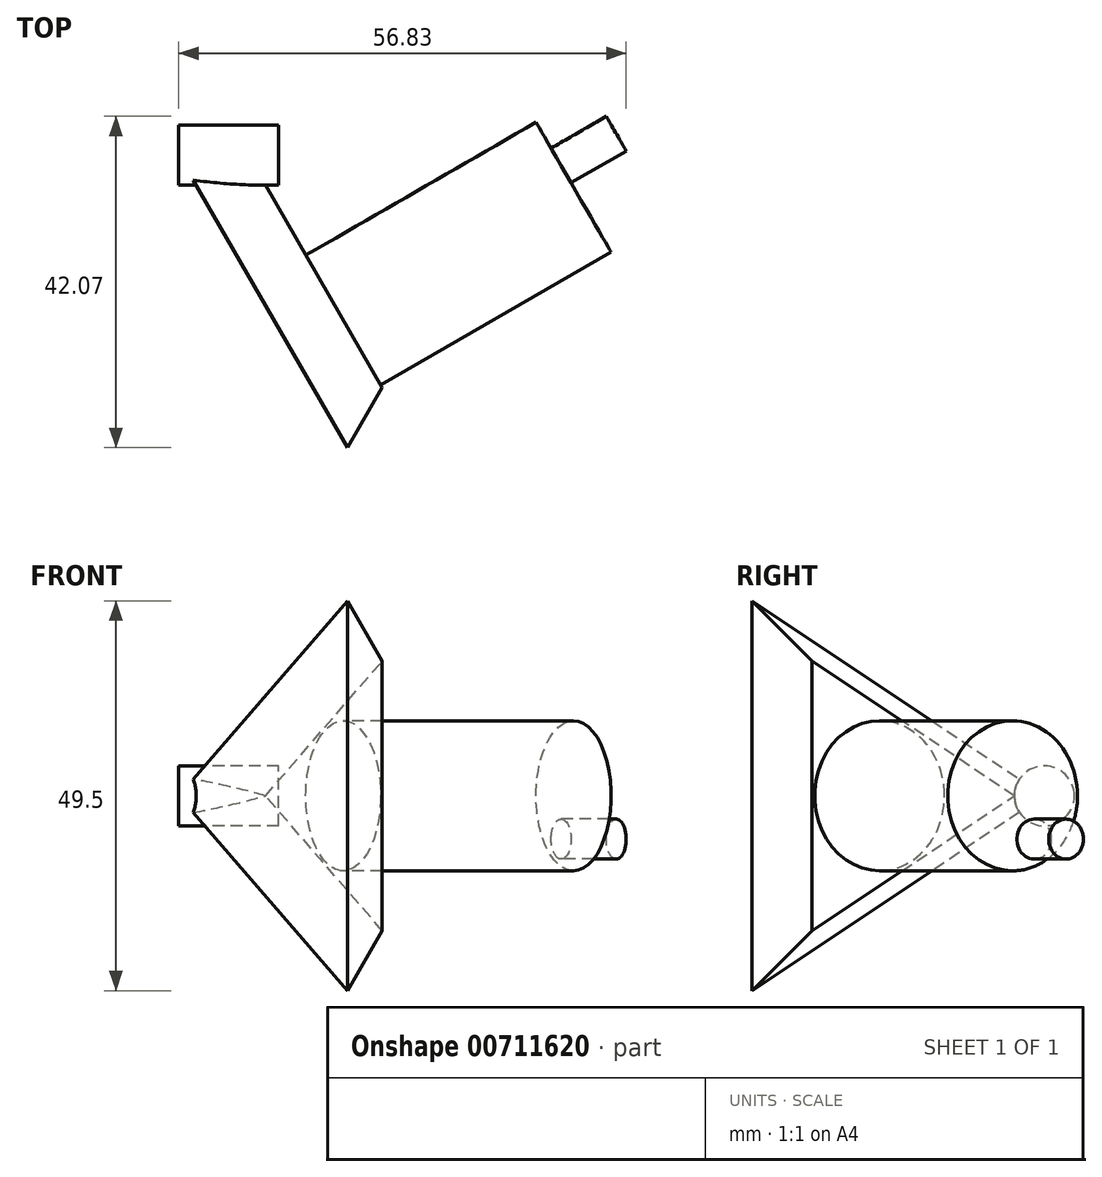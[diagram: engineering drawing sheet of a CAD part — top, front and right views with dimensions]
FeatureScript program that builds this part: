
annotation { "Feature Type Name" : "Feature", "Feature Type Description" : "" }
export const myFeature = defineFeature(function(context is Context, id is Id, definition is map)
    precondition{}
    {
        {
            var Q0;
            Q0=qCreatedBy(makeId("Top.planeOp"),FACE);
            var sketch = newSketch(context, id + "F0", { "sketchPlane" : qUnion([Q0])});
            skArc(sketch, "E0", {"start": v(0, 0) * mm, "mid": v(2.6, -19.72) * mm, "end": v(10.2, -38.1) * mm});
            skLineSegment(sketch, "E1", {"start": v(10.2, -38.1) * mm, "end": v(76.2, 0) * mm, "construction": true});
            skSolve(sketch);
        }
        {
            var Q0;
            Q0=qCreatedBy(makeId("Right.planeOp"),FACE);
            cPlane(context, id + "F1", {"entities" : qUnion([Q0]), "cplaneType" : CPlaneType.OFFSET, "offset" : 19.05 * mm, "width" : 152.4 * mm, "height" : 152.4 * mm});
        }
        {
            var Q0;
            Q0=qCreatedBy(id+"F1.planeOp",FACE);
            var sketch = newSketch(context, id + "F2", { "sketchPlane" : qUnion([Q0])});
            skCircle(sketch, "E2", {"center": v(0, 0) * mm, "radius": 3.81 * mm});
            skSolve(sketch);
        }
        {
            var Q0;
            Q0=qCreatedBy(makeId("Top.planeOp"),FACE);
            var sketch = newSketch(context, id + "F3", { "sketchPlane" : qUnion([Q0])});
            skLineSegment(sketch, "E3", {"start": v(19.05, 0) * mm, "end": v(33.34, -24.75) * mm});
            skLineSegment(sketch, "E4", {"start": v(33.34, -24.75) * mm, "end": v(76.2, 0) * mm, "construction": true});
            skLineSegment(sketch, "E5", {"start": v(76.2, 0) * mm, "end": v(19.05, 0) * mm, "construction": true});
            skSolve(sketch);
        }
        {
            var Q0;
            Q0=qCreatedBy(makeId("Top.planeOp"),FACE);
            var Q1;
            Q1=sQuery(id+"F3.wireOp",EDGE,"E3");
            cPlane(context, id + "F4", {"entities" : qUnion([Q0, Q1]), "cplaneType" : CPlaneType.LINE_ANGLE, "offset" : 25.4 * mm, "angle" : 90 * degree, "width" : 152.4 * mm, "height" : 152.4 * mm});
        }
        {
            var Q0;
            Q0=qCreatedBy(id+"F4.planeOp",FACE);
            var sketch = newSketch(context, id + "F5", { "sketchPlane" : qUnion([Q0])});
            skCircle(sketch, "E6.cCircle", {"center": v(-38.1, 0) * mm, "radius": 14.29 * mm, "construction": true});
            skLineSegment(sketch, "E6.0", {"start": v(-9.53, 0) * mm, "end": v(-52.39, -24.75) * mm});
            skLineSegment(sketch, "E6.1", {"start": v(-52.39, -24.75) * mm, "end": v(-52.39, 24.75) * mm});
            skLineSegment(sketch, "E6.2", {"start": v(-52.39, 24.75) * mm, "end": v(-9.53, 0) * mm});
            skPoint(sketch, "E6.0.midPoint", {"position": v(-30.96, -12.37) * mm});
            skSolve(sketch);
        }
        {
            var Q0;
            Q0=makeQuery(id+"F5.imprint","IMPRINT",FACE,{"disambiguationData":[TD([[makeQuery(id+"F5.imprint","IMPRINT",EDGE,{"derivedFrom":sQuery(id+"F5.wireOp",EDGE,"E6.0")}),-1.0]])]});
            extrude(context, id + "F6", {"entities" : qUnion([Q0]), "depth" : 7.62 * mm, "offsetDistance" : 25.4 * mm});
        }
        {
            var Q0;
            Q0=makeQuery(id+"F6.opExtrude","CAP_FACE",FACE,{"disambiguationData":[OSD([sQuery(id+"F5.wireOp",EDGE,"E6.0"),sQuery(id+"F5.wireOp",EDGE,"E6.1"),sQuery(id+"F5.wireOp",EDGE,"E6.2")])],"isStart":false});
            chamfer(context, id + "F7", {"entities" : qUnion([Q0]), "chamferType" : ChamferType.OFFSET_ANGLE, "width" : 7.62 * mm, "oppositeDirection" : false, "angle" : 30 * degree, "tangentPropagation" : true});
        }
        {
            var Q0;
            Q0 = qSketchRegion(id + "F2", true);
            var Q1;
            Q1=sQuery(id+"F2.wireOp",EDGE,"E2");
            var Q2;
            Q2=makeQuery(id+"F6.opExtrude","CAP_FACE",FACE,{"disambiguationData":[OSD([sQuery(id+"F5.wireOp",EDGE,"E6.0"),sQuery(id+"F5.wireOp",EDGE,"E6.1"),sQuery(id+"F5.wireOp",EDGE,"E6.2")])],"isStart":false});
            extrude(context, id + "F8", {"entities" : qUnion([Q0]), "operationType" : NewBodyOperationType.ADD, "surfaceEntities" : qUnion([Q1]), "depth" : 12.7 * mm, "endBoundEntityFace" : qUnion([Q2]), "offsetDistance" : 25.4 * mm});
        }
        {
            var Q0;
            Q0=makeQuery(id+"F6.opExtrude","CAP_FACE",FACE,{"disambiguationData":[OSD([sQuery(id+"F5.wireOp",EDGE,"E6.0"),sQuery(id+"F5.wireOp",EDGE,"E6.1"),sQuery(id+"F5.wireOp",EDGE,"E6.2")])],"isStart":false});
            var sketch = newSketch(context, id + "F9", { "sketchPlane" : qUnion([Q0])});
            skCircle(sketch, "E7", {"center": v(-38.1, 0) * mm, "radius": 9.53 * mm});
            skSolve(sketch);
        }
        {
            var Q0;
            Q0 = qSketchRegion(id + "F9", true);
            var Q1;
            Q1=sQuery(id+"F9.wireOp",EDGE,"E7");
            extrude(context, id + "F10", {"entities" : qUnion([Q0]), "operationType" : NewBodyOperationType.ADD, "surfaceEntities" : qUnion([Q1]), "depth" : 33.78 * mm, "offsetDistance" : 25.4 * mm});
        }
        {
            var Q0;
            Q0=makeQuery(id+"F10.opExtrude","CAP_FACE",FACE,{"disambiguationData":[OSD([sQuery(id+"F9.wireOp",EDGE,"E7")])],"isStart":false});
            var sketch = newSketch(context, id + "F11", { "sketchPlane" : qUnion([Q0])});
            skCircle(sketch, "E8", {"center": v(-38.1, 0) * mm, "radius": 6.35 * mm, "construction": true});
            skCircle(sketch, "E9", {"center": v(-34.93, -5.5) * mm, "radius": 2.54 * mm});
            skLineSegment(sketch, "E10.0", {"start": v(-47.99, -17.13) * mm, "end": v(-18.32, 0) * mm, "construction": true});
            skLineSegment(sketch, "E11", {"start": v(-33.16, -8.56) * mm, "end": v(-46.74, 14.97) * mm, "construction": true});
            skSolve(sketch);
        }
        {
            var Q0;
            Q0 = qSketchRegion(id + "F11", true);
            var Q1;
            Q1=sQuery(id+"F11.wireOp",EDGE,"E9");
            var Q2;
            Q2=sQuery(id+"F0.wireOp",VERTEX,"E0.center");
            extrude(context, id + "F12", {"entities" : qUnion([Q0]), "operationType" : NewBodyOperationType.ADD, "surfaceEntities" : qUnion([Q1]), "endBound" : BoundingType.UP_TO_VERTEX, "depth" : 25.4 * mm, "endBoundEntityVertex" : qUnion([Q2]), "offsetDistance" : 25.4 * mm});
        }
    });
